FCSTD DOCUMENT  (FreeCAD 0.16R6706 (Git))
Label: tejado
License: All rights reserved
LicenseURL: http://en.wikipedia.org/wiki/All_rights_reserved
objects: Part::Box×29, Part::Cut×27, Part::FeaturePython×21, Part::Fillet×6, Part::MultiFuse×6, Part::Mirroring×6, Sketcher::SketchObject×4, PartDesign::Pad×4, Part::Thickness×2, Part::Cone×1, Part::Cylinder×1
note: 111 computed .brp shape members not serialized (recipe doc carries the construction recipe); baked Part::Feature solids carry a one-line shape summary decoded from their .brp

FEATURE [Part::Box] Box  label="bloque_tejado_base"
  Height = 120
  Length = 144
  Width = 144
FEATURE [Part::Box] Box001  label="bloque_tejado_resta_norte"
  Height = 70
  Length = 144
  Placement = pos=(0,0,0) rot=(0,-1,0;0.959931rad)
  Width = 144
FEATURE [Part::Box] Box002  label="bloque_tejado_resta_este"
  Height = 70
  Length = 144
  Placement = pos=(0,0,0) rot=(1,0,0;1.309rad)
  Width = 144
FEATURE [Part::Box] Box003  label="bloque_tejado_resta_sur"
  Height = 70
  Length = 144
  Placement = pos=(61.405,0,117.958) rot=(0,1,0;0.959931rad)
  Width = 144
FEATURE [Part::Box] Box004  label="bloque_tejado_resta_oeste"
  Height = 70
  Length = 144
  Placement = pos=(0,106.73,139.093) rot=(-1,0,0;1.309rad)
  Width = 144
FEATURE [Part::Cut] Cut
  Base = -> Box
  Tool = -> Box001
FEATURE [Part::Cut] Cut001
  Base = -> Cut
  Tool = -> Box002
FEATURE [Part::Cut] Cut002
  Base = -> Cut001
  Tool = -> Box003
FEATURE [Part::Cut] Cut003  label="tejado_principal"
  Base = -> Cut002
  Tool = -> Box004
FEATURE [Part::Thickness] Thickness  label="tejado_principal_vaciado"
  Faces = -> Cut003 [Face1]
  Intersection = false
  Join = 0
  Mode = 0
  Placement = pos=(14,14,6.4) rot=(0,0,1;0rad)
  SelfIntersection = false
  Value = -2
FEATURE [Part::Box] Box005  label="bloque_faldon_base"
  Height = 70
  Length = 172
  Width = 172
FEATURE [Part::Box] Box006  label="bloque_faldon_resta_norte"
  Height = 70
  Length = 172
  Placement = pos=(0,0,0) rot=(1,0,0;0.436332rad)
  Width = 172
FEATURE [Part::Box] Box007  label="bloque_faldon_resta_este"
  Height = 70
  Length = 172
  Placement = pos=(0,0,0) rot=(0,-1,0;0.436332rad)
  Width = 172
FEATURE [Part::Box] Box008  label="bloque_faldon_resta_sur"
  Height = 70
  Length = 172
  Placement = pos=(0,16.1151,72.6903) rot=(-1,0,0;0.436332rad)
  Width = 172
FEATURE [Part::Box] Box009  label="bloque_faldon_resta_oeste"
  Height = 70
  Length = 172
  Placement = pos=(16.1151,0,72.6903) rot=(0,1,0;0.436332rad)
  Width = 172
FEATURE [Part::Cut] Cut004
  Base = -> Box005
  Tool = -> Box006
FEATURE [Part::Cut] Cut005
  Base = -> Cut004
  Tool = -> Box007
FEATURE [Part::Cut] Cut006
  Base = -> Cut005
  Tool = -> Box008
FEATURE [Part::Cut] Cut007  label="faldones"
  Base = -> Cut006
  Tool = -> Box009
FEATURE [Part::Thickness] Thickness001  label="no_op"
  Faces = -> Cut007 [Face1]
  Intersection = false
  Join = 0
  Mode = 0
  SelfIntersection = false
  Value = 0
FEATURE [Part::Box] Box010  label="bloque_faldon_resta_interior"
  Height = 200
  Length = 138
  Placement = pos=(17,17,-10) rot=(0,0,1;0rad)
  Width = 138
FEATURE [Part::Cut] Cut008  label="faldones_vaciado_interior"
  Base = -> Thickness001
  Tool = -> Box010
FEATURE [Part::Box] Box011  label="bloque_faldon_resta_muesca_norte"
  Height = 10
  Length = 7
  Placement = pos=(0,0,-3) rot=(0,0,1;0rad)
  Width = 5
FEATURE [Part::Box] Box012  label="bloque_faldon_resta_muesca_sur"
  Height = 10
  Length = 7
  Placement = pos=(165,0,-3) rot=(0,0,1;0rad)
  Width = 5
FEATURE [Part::Cut] Cut009  label="faldones_con_muesca_1"
  Base = -> Cut008
  Tool = -> Box011
FEATURE [Part::Cut] Cut010  label="faldones_con_muescas"
  Base = -> Cut009
  Tool = -> Box012
FEATURE [Part::FeaturePython] Array002  label="tejas"  # Draft array (typed FeaturePython)
  Angle = 360
  ArrayType = 0
  Axis = (0,0,1)
  Center = (0,0,0)
  Fuse = false
  IntervalAxis = (0,0,0)
  IntervalX = (1,0,0)
  IntervalY = (0,10.5,0)
  IntervalZ = (0,0,0)
  NumberPolar = 1
  NumberX = 1
  NumberY = 12
  NumberZ = 1
FEATURE [Sketcher::SketchObject] Sketch004
  Placement = pos=(9,10.5,0) rot=(0,0,1;3.14159rad)
  sketch-geometry (4):
    g0: LineSegment StartX=0 StartY=0 StartZ=0 EndX=4.1e-11 EndY=6 EndZ=0
    g1: LineSegment StartX=0 StartY=0 StartZ=0 EndX=9 EndY=0 EndZ=0
    g2: LineSegment StartX=9 StartY=0 StartZ=0 EndX=9 EndY=6 EndZ=0
    g3: ArcOfCircle CenterX=4.5 CenterY=5.99998 CenterZ=0 NormalX=0 NormalY=0 NormalZ=1 Radius=4.5 StartAngle=4.27504e-06 EndAngle=3.14159
  constraints (12):
    c: Coincident(g0,g-1)
    c: PointOnObject(g0,g-2)
    c: Coincident(g1,g-1)
    c: Horizontal(g1)
    c: Vertical(g2)
    c: Equal(g2,g0)
    c: Coincident(g3,g0)
    c: Coincident(g3,g2)
    c: DistanceX(g1) = 9
    c: Coincident(g1,g2)
    c: DistanceY(g0) = 6
    c: Radius(g3) = 4.5
FEATURE [PartDesign::Pad] Pad004  label="teja004"
  Length = 2
  Length2 = 100
  Placement = pos=(9,10.5,0) rot=(0,0,1;3.14159rad)
  Sketch = -> Sketch004
  Type = 0
FEATURE [Part::Fillet] Fillet004  label="teja_con_fillet004"
  Base = -> Pad004
  Edges = 4 edges r=0.5: [Edge4,Edge7,Edge10,Edge12]
  Placement = pos=(0,0.102185,1.46132) rot=(-1,0,0;0.139626rad)
FEATURE [Part::FeaturePython] Array008  label="fila_tejas_par"  # Draft array (typed FeaturePython)
  Angle = 360
  ArrayType = 0
  Axis = (1,0,0)
  Base = -> Fillet004
  Center = (0,0,0)
  Fuse = false
  IntervalAxis = (0,0,0)
  IntervalX = (9.5,0,0)
  IntervalY = (0,11,0)
  IntervalZ = (0,0,0)
  NumberPolar = 1
  NumberX = 20
  NumberY = 12
  NumberZ = 1
FEATURE [Sketcher::SketchObject] Sketch005
  Placement = pos=(9,10.5,0) rot=(0,0,1;3.14159rad)
  sketch-geometry (4):
    g0: LineSegment StartX=0 StartY=0 StartZ=0 EndX=4.1e-11 EndY=6 EndZ=0
    g1: LineSegment StartX=0 StartY=0 StartZ=0 EndX=9 EndY=0 EndZ=0
    g2: LineSegment StartX=9 StartY=0 StartZ=0 EndX=9 EndY=6 EndZ=0
    g3: ArcOfCircle CenterX=4.5 CenterY=5.99998 CenterZ=0 NormalX=0 NormalY=0 NormalZ=1 Radius=4.5 StartAngle=4.27504e-06 EndAngle=3.14159
  constraints (12):
    c: Coincident(g0,g-1)
    c: PointOnObject(g0,g-2)
    c: Coincident(g1,g-1)
    c: Horizontal(g1)
    c: Vertical(g2)
    c: Equal(g2,g0)
    c: Coincident(g3,g0)
    c: Coincident(g3,g2)
    c: DistanceX(g1) = 9
    c: Coincident(g1,g2)
    c: DistanceY(g0) = 6
    c: Radius(g3) = 4.5
FEATURE [PartDesign::Pad] Pad005  label="teja005"
  Length = 2
  Length2 = 100
  Placement = pos=(9,10.5,0) rot=(0,0,1;3.14159rad)
  Sketch = -> Sketch005
  Type = 0
FEATURE [Part::Fillet] Fillet005  label="teja_con_fillet005"
  Base = -> Pad005
  Edges = 4 edges r=0.5: [Edge4,Edge7,Edge10,Edge12]
  Placement = pos=(0,0.102185,1.46132) rot=(-1,0,0;0.139626rad)
FEATURE [Part::FeaturePython] Array009  label="fila_tejas_impar"  # Draft array (typed FeaturePython)
  Angle = 360
  ArrayType = 0
  Axis = (1,0,0)
  Base = -> Fillet005
  Center = (0,0,0)
  Fuse = false
  IntervalAxis = (0,0,0)
  IntervalX = (9.5,0,0)
  IntervalY = (0,11,0)
  IntervalZ = (0,0,0)
  NumberPolar = 1
  NumberX = 20
  NumberY = 12
  NumberZ = 1
  Placement = pos=(-4.75,6,0) rot=(0,0,1;0rad)
FEATURE [Part::Box] Box020  label="Cube020"
  Height = 200
  Length = 200
  Placement = pos=(10,0,0) rot=(0,-1,0;0.959931rad)
  Width = 200
FEATURE [Part::MultiFuse] Fusion  label="tejado_sin_tejas_con_faldon"
  Shapes = -> [Thickness,Cut010]
FEATURE [Part::Box] Box022  label="Cube"
  Height = 200
  Length = 200
  Placement = pos=(-190,0,0) rot=(0,0,1;0rad)
  Width = 200
FEATURE [Part::MultiFuse] Fusion002  label="bloque_resta_este"
  Shapes = -> [Box020,Box022]
FEATURE [Part::FeaturePython] Clone001  label="bloque_resta_oeste"  # Draft clone (typed FeaturePython)
  Objects = -> [Fusion002]
  Placement = pos=(172,200,0) rot=(0,0,1;3.14159rad)
  Scale = (1,1,1)
FEATURE [Part::MultiFuse] Fusion003  label="fila_doble_tejas"
  Placement = pos=(0,16,7.6) rot=(1,0,0;1.309rad)
  Shapes = -> [Array009,Array008]
FEATURE [Sketcher::SketchObject] Sketch006
  Placement = pos=(9,10.5,0) rot=(0,0,1;3.14159rad)
  sketch-geometry (4):
    g0: LineSegment StartX=0 StartY=0 StartZ=0 EndX=4.1e-11 EndY=6 EndZ=0
    g1: LineSegment StartX=0 StartY=0 StartZ=0 EndX=9 EndY=0 EndZ=0
    g2: LineSegment StartX=9 StartY=0 StartZ=0 EndX=9 EndY=6 EndZ=0
    g3: ArcOfCircle CenterX=4.5 CenterY=5.99998 CenterZ=0 NormalX=0 NormalY=0 NormalZ=1 Radius=4.5 StartAngle=4.27504e-06 EndAngle=3.14159
  constraints (12):
    c: Coincident(g0,g-1)
    c: PointOnObject(g0,g-2)
    c: Coincident(g1,g-1)
    c: Horizontal(g1)
    c: Vertical(g2)
    c: Equal(g2,g0)
    c: Coincident(g3,g0)
    c: Coincident(g3,g2)
    c: DistanceX(g1) = 9
    c: Coincident(g1,g2)
    c: DistanceY(g0) = 6
    c: Radius(g3) = 4.5
FEATURE [PartDesign::Pad] Pad006  label="teja006"
  Length = 2
  Length2 = 100
  Placement = pos=(9,10.5,0) rot=(0,0,1;3.14159rad)
  Sketch = -> Sketch006
  Type = 0
FEATURE [Part::Fillet] Fillet006  label="teja_con_fillet006"
  Base = -> Pad006
  Edges = 4 edges r=0.5: [Edge4,Edge7,Edge10,Edge12]
  Placement = pos=(0,0.102185,1.46132) rot=(-1,0,0;0.139626rad)
FEATURE [Part::FeaturePython] Array010  label="fila_tejas_par001"  # Draft array (typed FeaturePython)
  Angle = 360
  ArrayType = 0
  Axis = (1,0,0)
  Base = -> Fillet006
  Center = (0,0,0)
  Fuse = false
  IntervalAxis = (0,0,0)
  IntervalX = (9.5,0,0)
  IntervalY = (0,11,0)
  IntervalZ = (0,0,0)
  NumberPolar = 1
  NumberX = 20
  NumberY = 12
  NumberZ = 1
FEATURE [Sketcher::SketchObject] Sketch007
  Placement = pos=(9,10.5,0) rot=(0,0,1;3.14159rad)
  sketch-geometry (4):
    g0: LineSegment StartX=0 StartY=0 StartZ=0 EndX=4.1e-11 EndY=6 EndZ=0
    g1: LineSegment StartX=0 StartY=0 StartZ=0 EndX=9 EndY=0 EndZ=0
    g2: LineSegment StartX=9 StartY=0 StartZ=0 EndX=9 EndY=6 EndZ=0
    g3: ArcOfCircle CenterX=4.5 CenterY=5.99998 CenterZ=0 NormalX=0 NormalY=0 NormalZ=1 Radius=4.5 StartAngle=4.27504e-06 EndAngle=3.14159
  constraints (12):
    c: Coincident(g0,g-1)
    c: PointOnObject(g0,g-2)
    c: Coincident(g1,g-1)
    c: Horizontal(g1)
    c: Vertical(g2)
    c: Equal(g2,g0)
    c: Coincident(g3,g0)
    c: Coincident(g3,g2)
    c: DistanceX(g1) = 9
    c: Coincident(g1,g2)
    c: DistanceY(g0) = 6
    c: Radius(g3) = 4.5
FEATURE [PartDesign::Pad] Pad007  label="teja007"
  Length = 2
  Length2 = 100
  Placement = pos=(9,10.5,0) rot=(0,0,1;3.14159rad)
  Sketch = -> Sketch007
  Type = 0
FEATURE [Part::Fillet] Fillet007  label="teja_con_fillet007"
  Base = -> Pad007
  Edges = 4 edges r=0.5: [Edge4,Edge7,Edge10,Edge12]
  Placement = pos=(0,0.102185,1.46132) rot=(-1,0,0;0.139626rad)
FEATURE [Part::FeaturePython] Array011  label="fila_tejas_impar001"  # Draft array (typed FeaturePython)
  Angle = 360
  ArrayType = 0
  Axis = (1,0,0)
  Base = -> Fillet007
  Center = (0,0,0)
  Fuse = false
  IntervalAxis = (0,0,0)
  IntervalX = (9.5,0,0)
  IntervalY = (0,11,0)
  IntervalZ = (0,0,0)
  NumberPolar = 1
  NumberX = 20
  NumberY = 12
  NumberZ = 1
  Placement = pos=(-4.75,6,0) rot=(0,0,1;0rad)
FEATURE [Part::Cut] Cut011  label="tejas_norte_un_corte"
  Base = -> Fusion003
  Tool = -> Fusion002
FEATURE [Part::Cut] Cut012  label="tejas_norte"
  Base = -> Cut011
  Tool = -> Clone001
FEATURE [Part::FeaturePython] Clone  label="tejas_sur"  # Draft clone (typed FeaturePython)
  Objects = -> [Cut012]
  Placement = pos=(172,172,0) rot=(0,0,1;3.14159rad)
  Scale = (1,1,1)
FEATURE [Part::FeaturePython] Clone002  label="fila_doble_tejas_2"  # Draft clone (typed FeaturePython)
  Objects = -> [Fusion003]
  Placement = pos=(16.5,190,7.5) rot=(0.419215,-0.419215,-0.805306;1.78566rad)
  Scale = (1,1,1)
FEATURE [Part::Box] Box023  label="Cube021"
  Height = 200
  Length = 200
  Placement = pos=(0,-180.685,51.7638) rot=(-1,0,0;0.261799rad)
  Width = 200
FEATURE [Part::Box] Box024  label="Cube022"
  Height = 200
  Length = 200
  Placement = pos=(0,-188,0) rot=(0,0,1;0rad)
  Width = 200
FEATURE [Part::MultiFuse] Fusion004  label="bloque_resta_norte"
  Shapes = -> [Box023,Box024]
FEATURE [Part::FeaturePython] Clone003  label="bloque_resta_sur"  # Draft clone (typed FeaturePython)
  Objects = -> [Fusion004]
  Placement = pos=(200,172,0) rot=(0,0,1;3.14159rad)
  Scale = (1,1,1)
FEATURE [Part::Cut] Cut013
  Base = -> Clone002
  Tool = -> Fusion004
FEATURE [Part::Cut] Cut014
  Base = -> Cut013
  Tool = -> Clone003
FEATURE [Part::Box] Box025  label="Cube023"
  Height = 200
  Length = 200
  Placement = pos=(0,0,109) rot=(0,0,1;0rad)
  Width = 200
FEATURE [Part::Cut] Cut015  label="tejas_este"
  Base = -> Cut014
  Tool = -> Box025
FEATURE [Part::FeaturePython] Clone004  label="tejas_oeste"  # Draft clone (typed FeaturePython)
  Objects = -> [Cut015]
  Placement = pos=(172,172,0) rot=(0,0,1;3.14159rad)
  Scale = (1,1,1)
FEATURE [Part::FeaturePython] Clone005  label="faldon_fila_doble_tejas"  # Draft clone (typed FeaturePython)
  Objects = -> [Fusion003]
  Placement = pos=(0,0.5,-1.3) rot=(1,0,0;0.436332rad)
  Scale = (1,1,1)
FEATURE [Part::Box] Box027  label="bloque_faldon_resta_este001"
  Height = 70
  Length = 172
  Placement = pos=(0,0,0) rot=(0,-1,0;0.436332rad)
  Width = 182
FEATURE [Part::Box] Box028  label="Cube024"
  Height = 70
  Length = 172
  Placement = pos=(-172,0,0) rot=(0,0,1;0rad)
  Width = 182
FEATURE [Part::MultiFuse] Fusion005  label="faldon_bloque_resta_tejas_este"
  Placement = pos=(0,-5,0) rot=(0,0,1;0rad)
  Shapes = -> [Box027,Box028]
FEATURE [Part::FeaturePython] Clone006  label="faldon_bloque_resta_tejas_oeste"  # Draft clone (typed FeaturePython)
  Objects = -> [Fusion005]
  Placement = pos=(172,177,0) rot=(0,0,1;3.14159rad)
  Scale = (1,1,1)
FEATURE [Part::Cut] Cut016
  Base = -> Clone005
  Tool = -> Fusion005
FEATURE [Part::Cut] Cut017  label="Cut019"
  Base = -> Cut016
  Tool = -> Clone006
FEATURE [Part::Box] Box029  label="bloque_faldon_resta_interior001"
  Height = 200
  Length = 138
  Placement = pos=(17,17,-10) rot=(0,0,1;0rad)
  Width = 138
FEATURE [Part::Cut] Cut018  label="faldon_tejas_norte_sin_muesca"
  Base = -> Cut017
  Tool = -> Box029
FEATURE [Part::FeaturePython] Clone007  label="faldon_tejas_sur"  # Draft clone (typed FeaturePython)
  Objects = -> [Cut018]
  Placement = pos=(172,172,0) rot=(0,0,1;3.14159rad)
  Scale = (1,1,1)
FEATURE [Part::FeaturePython] Clone008  label="faldon_tejas_este_sin_muesca"  # Draft clone (typed FeaturePython)
  Objects = -> [Cut018]
  Placement = pos=(172,0,0) rot=(0,0,1;1.5708rad)
  Scale = (1,1,1)
FEATURE [Part::FeaturePython] Clone009  label="faldon_tejas_oeste_sin_muesca"  # Draft clone (typed FeaturePython)
  Objects = -> [Cut018]
  Placement = pos=(0,172,0) rot=(0,0,-1;1.5708rad)
  Scale = (1,1,1)
FEATURE [Part::Box] Box032  label="bloque_faldon_resta_muesca_norte002"
  Height = 10
  Length = 10
  Placement = pos=(-3,-5,-3) rot=(0,0,1;0rad)
  Width = 10
FEATURE [Part::Box] Box033  label="bloque_faldon_resta_muesca_sur002"
  Height = 10
  Length = 10
  Placement = pos=(165,-5,-3) rot=(0,0,1;0rad)
  Width = 10
FEATURE [Part::Box] Box034  label="bloque_faldon_resta_muesca_sur003"
  Height = 10
  Length = 10
  Placement = pos=(165,-5,-3) rot=(0,0,1;0rad)
  Width = 10
FEATURE [Part::Box] Box035  label="bloque_faldon_resta_muesca_norte003"
  Height = 10
  Length = 10
  Placement = pos=(-3,-5,-3) rot=(0,0,1;0rad)
  Width = 10
FEATURE [Part::Cut] Cut019  label="faldon_tejas_oeste"
  Base = -> Clone009
  Tool = -> Box032
FEATURE [Part::Cut] Cut020
  Base = -> Cut018
  Tool = -> Box035
FEATURE [Part::Cut] Cut021  label="faldon_tejas_norte"
  Base = -> Cut020
  Tool = -> Box034
FEATURE [Part::Cut] Cut022  label="faldon_tejas_este"
  Base = -> Clone008
  Tool = -> Box033
FEATURE [Part::Cone] Cone
  Angle = 360
  Height = 11
  Radius1 = 5
  Radius2 = 4
FEATURE [Part::Box] Box036  label="Cube025"
  Height = 20
  Length = 20
  Placement = pos=(0,-10,0) rot=(0,0,1;0rad)
  Width = 20
FEATURE [Part::Cut] Cut023  label="teja_curva_sin_fillet"
  Base = -> Cone
  Placement = pos=(0,0,0) rot=(0,1,0;1.5708rad)
  Tool = -> Box036
FEATURE [Part::Fillet] Fillet  label="teja_curva"
  Base = -> Cut023
  Edges = 1 edges r=1: [Edge3]
FEATURE [Part::FeaturePython] Array  label="remate_tejas_faldon_NE"  # Draft array (typed FeaturePython)
  Angle = 360
  ArrayType = 0
  Axis = (0,0,1)
  Base = -> Fillet
  Center = (0,0,0)
  Fuse = false
  IntervalAxis = (0,0,0)
  IntervalX = (10,0,0)
  IntervalY = (0,1,0)
  IntervalZ = (0,0,0)
  NumberPolar = 1
  NumberX = 2
  NumberY = 1
  NumberZ = 1
  Placement = pos=(3.32609,2.65169,0.394417) rot=(0.152676,-0.349377,0.92446;0.854148rad)
FEATURE [Part::FeaturePython] Clone010  label="clon_teja_curva"  # Draft clone (typed FeaturePython)
  Objects = -> [Fillet]
  Scale = (1,1,1)
FEATURE [Part::FeaturePython] Array012  label="remate_tejas_NE"  # Draft array (typed FeaturePython)
  Angle = 360
  ArrayType = 0
  Axis = (0,0,1)
  Base = -> Clone010
  Center = (0,0,0)
  Fuse = false
  IntervalAxis = (0,0,0)
  IntervalX = (9.5,0,0)
  IntervalY = (0,1,0)
  IntervalZ = (0,0,0)
  NumberPolar = 1
  NumberX = 13
  NumberY = 1
  NumberZ = 1
  Placement = pos=(16.2827,15.4574,6.66918) rot=(0.459946,-0.760073,0.459063;1.11348rad)
FEATURE [Part::FeaturePython] Clone011  label="Clone of teja_curva"  # Draft clone (typed FeaturePython)
  Objects = -> [Fillet]
  Scale = (1,1,1)
FEATURE [Part::FeaturePython] Array013  label="4_tejas_curvas"  # Draft array (typed FeaturePython)
  Angle = 360
  ArrayType = 0
  Axis = (0,0,1)
  Base = -> Clone011
  Center = (0,0,0)
  Fuse = false
  IntervalAxis = (0,0,0)
  IntervalX = (10,0,0)
  IntervalY = (0,1,0)
  IntervalZ = (0,0,0)
  NumberPolar = 1
  NumberX = 4
  NumberY = 1
  NumberZ = 1
FEATURE [Part::Box] Box037  label="Cube026"
  Height = 20
  Length = 20
  Placement = pos=(0,-10,0) rot=(0,0,1;0rad)
  Width = 20
FEATURE [Part::Cylinder] Cylinder
  Angle = 360
  Height = 11
  Radius = 5
FEATURE [Part::Cut] Cut024
  Base = -> Cylinder
  Placement = pos=(0,0,0) rot=(0,1,0;1.5708rad)
  Tool = -> Box037
FEATURE [Part::Fillet] Fillet008  label="teja_curva_central"
  Base = -> Cut024
  Edges = 2 edges r=1: [Edge1,Edge3]
  Placement = pos=(40,0,0) rot=(0,0,1;0rad)
FEATURE [Part::FeaturePython] Clone012  label="4_tejas_curvas_b"  # Draft clone (typed FeaturePython)
  Objects = -> [Array013]
  Placement = pos=(91,0,0) rot=(0,0,1;3.14159rad)
  Scale = (1,1,1)
FEATURE [Part::MultiFuse] Fusion006  label="remate_tejas_cenit"
  Placement = pos=(86,40.5523,106.227) rot=(0,0,1;1.5708rad)
  Shapes = -> [Array013,Clone012,Fillet008]
FEATURE [Part::Mirroring] Part__Mirroring004  label="remate_tejas_NW"
  Base = (0,0,0)
  Normal = (1,0,0)
  Placement = pos=(172,0,0) rot=(0,0,1;0rad)
  Source = -> Array012
FEATURE [Part::Mirroring] Part__Mirroring005  label="remate_tejas_SW"
  Base = (0,0,0)
  Normal = (0,1,0)
  Placement = pos=(0,172,0) rot=(0,0,1;0rad)
  Source = -> Part__Mirroring004
FEATURE [Part::Mirroring] Part__Mirroring006  label="remate_tejas_SE"
  Base = (0,0,0)
  Normal = (1,0,0)
  Placement = pos=(172,0,0) rot=(0,0,1;0rad)
  Source = -> Part__Mirroring005
FEATURE [Part::Mirroring] Part__Mirroring  label="remate_tejas_faldon_NW"
  Base = (0,0,0)
  Normal = (1,0,0)
  Placement = pos=(172,0,0) rot=(0,0,1;0rad)
  Source = -> Array
FEATURE [Part::Mirroring] Part__Mirroring007  label="remate_tejas_faldon_SW"
  Base = (0,0,0)
  Normal = (0,1,0)
  Placement = pos=(0,172,0) rot=(0,0,1;0rad)
  Source = -> Part__Mirroring
FEATURE [Part::Mirroring] Part__Mirroring008  label="remate_tejas_faldon_SE"
  Base = (0,0,0)
  Normal = (1,0,0)
  Placement = pos=(172,0,0) rot=(0,0,1;0rad)
  Source = -> Part__Mirroring007
FEATURE [Part::Box] Box038  label="bloque_faldon_resta_muesca_norte004"
  Height = 10
  Length = 10
  Placement = pos=(-3,-5,-3) rot=(0,0,1;0rad)
  Width = 10
FEATURE [Part::Box] Box039  label="bloque_faldon_resta_muesca_sur004"
  Height = 10
  Length = 10
  Placement = pos=(165,-5,-3) rot=(0,0,1;0rad)
  Width = 10
FEATURE [Part::Cut] Cut025  label="remate_tejas_faldon_NW_con_muesca"
  Base = -> Part__Mirroring
  Tool = -> Box039
FEATURE [Part::Cut] Cut026  label="remate_tejas_faldon_NE_con_muesca"
  Base = -> Array
  Tool = -> Box038
